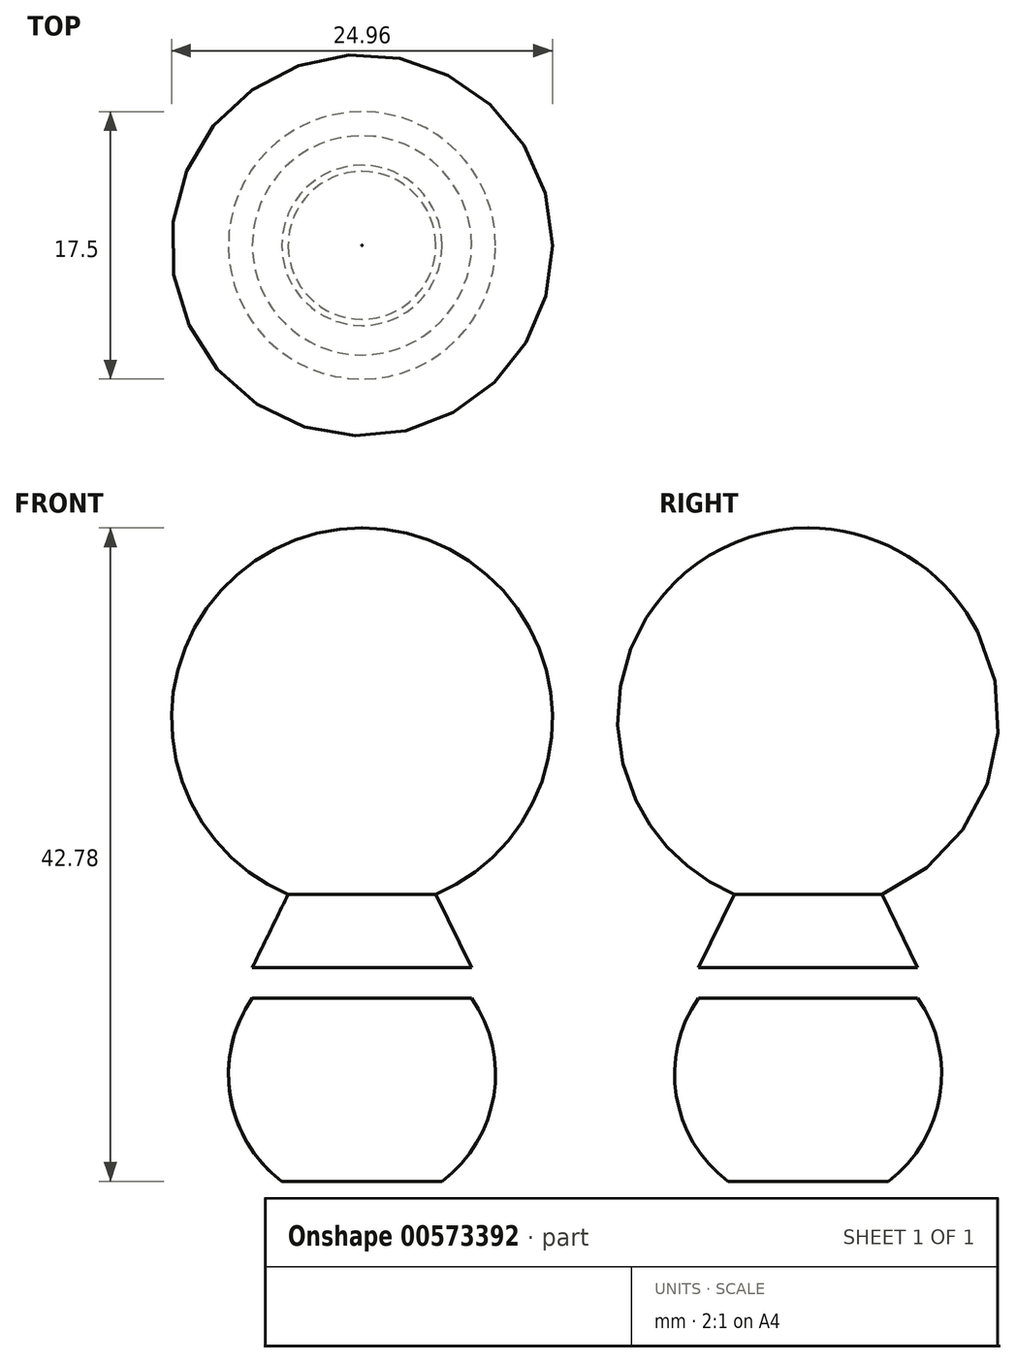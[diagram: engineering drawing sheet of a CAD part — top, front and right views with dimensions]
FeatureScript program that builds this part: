
annotation { "Feature Type Name" : "Feature", "Feature Type Description" : "" }
export const myFeature = defineFeature(function(context is Context, id is Id, definition is map)
    precondition{}
    {
        {
            var Q0;
            Q0=qCreatedBy(makeId("Front.planeOp"),FACE);
            var sketch = newSketch(context, id + "F0", { "sketchPlane" : qUnion([Q0])});
            skLineSegment(sketch, "E0.trimOffspring", {"start": v(0.01, 0) * mm, "end": v(5.26, 0) * mm});
            skLineSegment(sketch, "E1.MirrorCS", {"start": v(0.01, 12) * mm, "end": v(0.01, 0) * mm});
            skArc(sketch, "E2.MirrorCS", {"start": v(7.2, 12) * mm, "mid": v(8.65, 5.61) * mm, "end": v(5.26, 0) * mm});
            skLineSegment(sketch, "E3.MirrorCS", {"start": v(7.2, 12) * mm, "end": v(0.01, 12) * mm});
            skLineSegment(sketch, "E4.bottom", {"start": v(0.01, 12) * mm, "end": v(7.2, 12) * mm});
            skLineSegment(sketch, "E4.top", {"start": v(0.01, 14) * mm, "end": v(7.2, 14) * mm});
            skLineSegment(sketch, "E4.right", {"start": v(7.2, 12) * mm, "end": v(7.2, 14) * mm});
            skArc(sketch, "E5", {"start": v(0.01, 17.8) * mm, "mid": v(12.49, 30.29) * mm, "end": v(0.01, 42.78) * mm});
            skLineSegment(sketch, "E6", {"start": v(0.01, 18.78) * mm, "end": v(4.85, 18.78) * mm});
            skLineSegment(sketch, "E7", {"start": v(4.85, 18.78) * mm, "end": v(7.2, 14) * mm});
            skLineSegment(sketch, "E8", {"start": v(0.01, 0) * mm, "end": v(0.01, 42.78) * mm});
            skSolve(sketch);
        }
        {
            var Q0;
            {var subQ0=sQuery(id+"F0.wireOp",EDGE,"E4.bottom");Q0=makeQuery(id+"F0.imprint","IMPRINT",FACE,{"disambiguationData":[TD([[makeQuery(id+"F0.imprint","IMPRINT",EDGE,{"derivedFrom":subQ0}),1.0]])]});}
            var Q1;
            {var subQ0=sQuery(id+"F0.wireOp",EDGE,"E0.trimOffspring");Q1=makeQuery(id+"F0.imprint","IMPRINT",FACE,{"disambiguationData":[TD([[makeQuery(id+"F0.imprint","IMPRINT",EDGE,{"derivedFrom":subQ0}),1.0]])]});}
            var Q2;
            {var subQ0=sQuery(id+"F0.wireOp",EDGE,"E4.top");Q2=makeQuery(id+"F0.imprint","IMPRINT",FACE,{"disambiguationData":[TD([[makeQuery(id+"F0.imprint","IMPRINT",EDGE,{"derivedFrom":subQ0}),1.0]])]});}
            var Q3;
            {var subQ3=sQuery(id+"F0.wireOp",EDGE,"E6");Q3=makeQuery(id+"F0.imprint","IMPRINT",FACE,{"disambiguationData":[TD([[makeQuery(id+"F0.imprint","IMPRINT",EDGE,{"derivedFrom":subQ3}),-1.0]])]});}
            var Q4;
            {var subQ3=sQuery(id+"F0.wireOp",EDGE,"E6");Q4=makeQuery(id+"F0.imprint","IMPRINT",FACE,{"disambiguationData":[TD([[makeQuery(id+"F0.imprint","IMPRINT",EDGE,{"derivedFrom":subQ3}),1.0]])]});}
            var Q5;
            Q5=sQuery(id+"F0.wireOp",EDGE,"E0.trimOffspring");
            var Q6;
            Q6=sQuery(id+"F0.wireOp",EDGE,"E7");
            var Q7;
            Q7=sQuery(id+"F0.wireOp",EDGE,"E4.bottom");
            var Q8;
            Q8=sQuery(id+"F0.wireOp",EDGE,"E4.top");
            var Q9;
            Q9=sQuery(id+"F0.wireOp",EDGE,"E5");
            var Q10;
            Q10=sQuery(id+"F0.wireOp",EDGE,"E6");
            var Q11;
            Q11=sQuery(id+"F0.wireOp",EDGE,"E4.right");
            var Q12;
            Q12=sQuery(id+"F0.wireOp",EDGE,"E2.MirrorCS");
            var Q13;
            Q13=sQuery(id+"F0.wireOp",EDGE,"E8");
            var Q14;
            Q14=sQuery(id+"F0.wireOp",EDGE,"E3.MirrorCS");
            var Q15;
            Q15=sQuery(id+"F0.wireOp",EDGE,"E1.MirrorCS");
            var Q16;
            Q16=sQuery(id+"F0.wireOp",EDGE,"E8");
            revolve(context, id + "F1", {"entities" : qUnion([Q0, Q1, Q2, Q3, Q4]), "surfaceEntities" : qUnion([Q5, Q6, Q7, Q8, Q9, Q10, Q11, Q12, Q13, Q14, Q15]), "axis" : qUnion([Q16]), "revolveType" : RevolveType.FULL});
        }
    });
